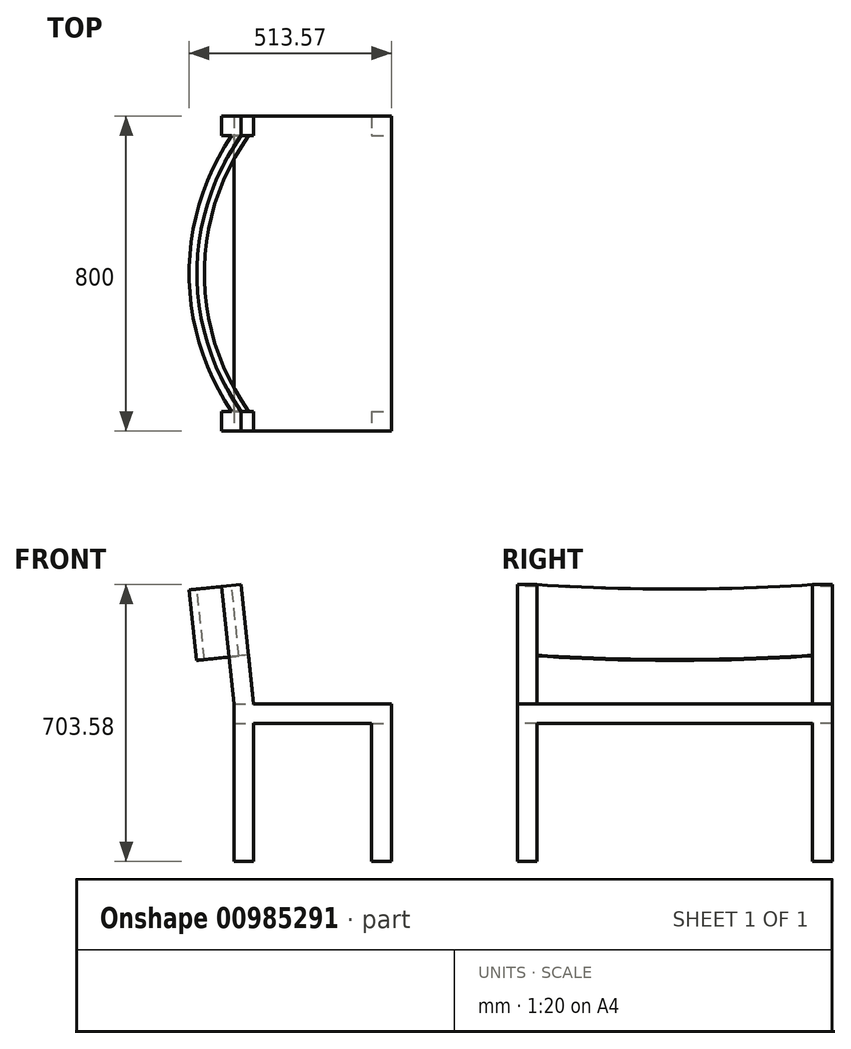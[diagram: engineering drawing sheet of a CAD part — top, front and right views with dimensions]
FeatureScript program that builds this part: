
annotation { "Feature Type Name" : "Feature", "Feature Type Description" : "" }
export const myFeature = defineFeature(function(context is Context, id is Id, definition is map)
    precondition{}
    {
        {
            var Q0;
            Q0=qCreatedBy(makeId("Top.planeOp"),FACE);
            var sketch = newSketch(context, id + "F0", { "sketchPlane" : qUnion([Q0])});
            skLineSegment(sketch, "E0.bottom", {"start": v(200, 400) * mm, "end": v(-200, 400) * mm});
            skLineSegment(sketch, "E0.top", {"start": v(200, -400) * mm, "end": v(-200, -400) * mm});
            skLineSegment(sketch, "E0.left", {"start": v(200, 400) * mm, "end": v(200, -400) * mm});
            skLineSegment(sketch, "E0.right", {"start": v(-200, 400) * mm, "end": v(-200, -400) * mm});
            skPoint(sketch, "E0.middle", {"position": v(0, 0) * mm});
            skSolve(sketch);
        }
        {
            var Q0;
            Q0=makeQuery(id+"F0.imprint","IMPRINT",FACE,{"disambiguationData":[TD([[makeQuery(id+"F0.imprint","IMPRINT",EDGE,{"derivedFrom":sQuery(id+"F0.wireOp",EDGE,"E0.bottom")}),1.0]])]});
            extrude(context, id + "F1", {"entities" : qUnion([Q0]), "depth" : 400 * mm, "offsetDistance" : 25 * mm});
        }
        {
            var Q0;
            Q0=makeQuery(id+"F1.opExtrude","SWEPT_FACE",FACE,{"disambiguationData":[OSD([sQuery(id+"F0.wireOp",EDGE,"E0.top")])]});
            var sketch = newSketch(context, id + "F2", { "sketchPlane" : qUnion([Q0])});
            skLineSegment(sketch, "E1.bottom", {"start": v(-150, 0) * mm, "end": v(150, 0) * mm});
            skLineSegment(sketch, "E1.top", {"start": v(-150, 350) * mm, "end": v(150, 350) * mm});
            skLineSegment(sketch, "E1.left", {"start": v(-150, 0) * mm, "end": v(-150, 350) * mm});
            skLineSegment(sketch, "E1.right", {"start": v(150, 0) * mm, "end": v(150, 350) * mm});
            skSolve(sketch);
        }
        {
            var Q0;
            Q0=makeQuery(id+"F2.imprint","IMPRINT",FACE,{"disambiguationData":[TD([[makeQuery(id+"F2.imprint","IMPRINT",EDGE,{"derivedFrom":sQuery(id+"F2.wireOp",EDGE,"E1.bottom")}),-1.0]])]});
            extrude(context, id + "F3", {"entities" : qUnion([Q0]), "operationType" : NewBodyOperationType.REMOVE, "endBound" : BoundingType.THROUGH_ALL, "oppositeDirection" : true, "depth" : 25 * mm, "offsetDistance" : 25 * mm});
        }
        {
            var Q0;
            Q0=makeQuery(id+"F1.opExtrude","SWEPT_FACE",FACE,{"disambiguationData":[OSD([sQuery(id+"F0.wireOp",EDGE,"E0.left")])]});
            var sketch = newSketch(context, id + "F4", { "sketchPlane" : qUnion([Q0])});
            skLineSegment(sketch, "E2.bottom", {"start": v(-350, 0) * mm, "end": v(350, 0) * mm});
            skLineSegment(sketch, "E2.top", {"start": v(-350, 350) * mm, "end": v(350, 350) * mm});
            skLineSegment(sketch, "E2.left", {"start": v(-350, 0) * mm, "end": v(-350, 350) * mm});
            skLineSegment(sketch, "E2.right", {"start": v(350, 0) * mm, "end": v(350, 350) * mm});
            skSolve(sketch);
        }
        {
            var Q0;
            Q0=makeQuery(id+"F4.imprint","IMPRINT",FACE,{"disambiguationData":[TD([[makeQuery(id+"F4.imprint","IMPRINT",EDGE,{"derivedFrom":sQuery(id+"F4.wireOp",EDGE,"E2.bottom")}),-1.0]])]});
            extrude(context, id + "F5", {"entities" : qUnion([Q0]), "operationType" : NewBodyOperationType.REMOVE, "endBound" : BoundingType.THROUGH_ALL, "oppositeDirection" : true, "depth" : 25 * mm, "offsetDistance" : 25 * mm});
        }
        {
            var Q0;
            Q0=makeQuery(id+"F1.opExtrude","CAP_FACE",FACE,{"disambiguationData":[OSD([sQuery(id+"F0.wireOp",EDGE,"E0.bottom"),sQuery(id+"F0.wireOp",EDGE,"E0.top"),sQuery(id+"F0.wireOp",EDGE,"E0.left"),sQuery(id+"F0.wireOp",EDGE,"E0.right")])],"isStart":false});
            var Q1;
            Q1=makeQuery(id+"F1.opExtrude","CAP_VERTEX",VERTEX,{"disambiguationData":[OSD([sQuery(id+"F0.wireOp",EDGE,"E0.top"),sQuery(id+"F0.wireOp",EDGE,"E0.left")])],"isStart":false});
            cPlane(context, id + "F6", {"entities" : qUnion([Q0, Q1]), "cplaneType" : CPlaneType.PLANE_POINT, "offset" : 25 * mm, "width" : 150 * mm, "height" : 150 * mm});
        }
        {
            var Q0;
            Q0=qCreatedBy(id+"F6.planeOp",FACE);
            var sketch = newSketch(context, id + "F7", { "sketchPlane" : qUnion([Q0])});
            skLineSegment(sketch, "E3", {"start": v(-200, -527.76) * mm, "end": v(-200, 626.76) * mm, "construction": true});
            skSolve(sketch);
        }
        {
            var Q0;
            Q0=makeQuery(id+"F1.opExtrude","SWEPT_FACE",FACE,{"disambiguationData":[OSD([sQuery(id+"F0.wireOp",EDGE,"E0.right")])]});
            var Q1;
            Q1=makeQuery(id+"F5.boolean.opBoolean","INTERSECT",VERTEX,{"derivedFrom":[makeQuery(id+"F1.opExtrude","SWEPT_FACE",FACE,{"disambiguationData":[OSD([sQuery(id+"F0.wireOp",EDGE,"E0.right")])]}),makeQuery(id+"F5.opExtrude","SWEPT_FACE",FACE,{"disambiguationData":[OSD([sQuery(id+"F4.wireOp",EDGE,"E2.top")])]}),makeQuery(id+"F5.opExtrude","SWEPT_FACE",FACE,{"disambiguationData":[OSD([sQuery(id+"F4.wireOp",EDGE,"E2.left")])]})]});
            cPlane(context, id + "F8", {"entities" : qUnion([Q0, Q1]), "cplaneType" : CPlaneType.PLANE_POINT, "offset" : 25 * mm, "width" : 150 * mm, "height" : 150 * mm});
        }
        {
            var Q0;
            Q0=sQuery(id+"F7.wireOp",EDGE,"E3");
            var Q1;
            Q1=qCreatedBy(id+"F8.planeOp",FACE);
            cPlane(context, id + "F9", {"entities" : qUnion([Q0, Q1]), "cplaneType" : CPlaneType.LINE_ANGLE, "offset" : 25 * mm, "angle" : 6 * degree, "oppositeDirection" : true, "width" : 150 * mm, "height" : 150 * mm});
        }
        {
            var Q0;
            Q0=qCreatedBy(id+"F9.planeOp",FACE);
            var sketch = newSketch(context, id + "F10", { "sketchPlane" : qUnion([Q0])});
            skLineSegment(sketch, "E4.bottom", {"start": v(400, 418.71) * mm, "end": v(-400, 418.71) * mm});
            skLineSegment(sketch, "E4.top", {"start": v(400, 718.71) * mm, "end": v(-400, 718.71) * mm});
            skLineSegment(sketch, "E4.left", {"start": v(400, 418.71) * mm, "end": v(400, 718.71) * mm});
            skLineSegment(sketch, "E4.right", {"start": v(-400, 418.71) * mm, "end": v(-400, 718.71) * mm});
            skSolve(sketch);
        }
        {
            var Q0;
            Q0=makeQuery(id+"F10.imprint","IMPRINT",FACE,{"disambiguationData":[TD([[makeQuery(id+"F10.imprint","IMPRINT",EDGE,{"derivedFrom":sQuery(id+"F10.wireOp",EDGE,"E4.bottom")}),-1.0]])]});
            extrude(context, id + "F11", {"entities" : qUnion([Q0]), "depth" : 50 * mm, "offsetDistance" : 25 * mm});
        }
        {
            var Q0;
            Q0=makeQuery(id+"F11.opExtrude","CAP_FACE",FACE,{"disambiguationData":[OSD([sQuery(id+"F10.wireOp",EDGE,"E4.bottom"),sQuery(id+"F10.wireOp",EDGE,"E4.top"),sQuery(id+"F10.wireOp",EDGE,"E4.left"),sQuery(id+"F10.wireOp",EDGE,"E4.right")])],"isStart":true});
            var sketch = newSketch(context, id + "F12", { "sketchPlane" : qUnion([Q0])});
            skLineSegment(sketch, "E5.bottom", {"start": v(-350, 418.71) * mm, "end": v(350, 418.71) * mm});
            skLineSegment(sketch, "E5.top", {"start": v(-350, 718.71) * mm, "end": v(350, 718.71) * mm});
            skLineSegment(sketch, "E5.left", {"start": v(-350, 418.71) * mm, "end": v(-350, 718.71) * mm});
            skLineSegment(sketch, "E5.right", {"start": v(350, 418.71) * mm, "end": v(350, 718.71) * mm});
            skSolve(sketch);
        }
        {
            var Q0;
            Q0=makeQuery(id+"F12.imprint","IMPRINT",FACE,{"disambiguationData":[TD([[makeQuery(id+"F12.imprint","IMPRINT",EDGE,{"derivedFrom":sQuery(id+"F12.wireOp",EDGE,"E5.bottom")}),1.0]])]});
            extrude(context, id + "F13", {"entities" : qUnion([Q0]), "operationType" : NewBodyOperationType.REMOVE, "endBound" : BoundingType.THROUGH_ALL, "oppositeDirection" : true, "depth" : 25 * mm, "offsetDistance" : 25 * mm});
        }
        {
            var Q0;
            {var subQ0=sQuery(id+"F10.wireOp",EDGE,"E4.right");var subQ3=sQuery(id+"F10.wireOp",EDGE,"E4.bottom");Q0=makeQuery(id+"F13.boolean.opBoolean","SPLIT",FACE,{"disambiguationData":[TD([makeQuery(id+"F11.opExtrude","SWEPT_FACE",FACE,{"disambiguationData":[OSD([subQ0])]})])],"derivedFrom":makeQuery(id+"F11.opExtrude","SWEPT_FACE",FACE,{"disambiguationData":[OSD([subQ3])]})});}
            var Q1;
            Q1=makeQuery(id+"F1.opExtrude","SWEPT_BODY",BODY,{"disambiguationData":[OSD([sQuery(id+"F0.wireOp",EDGE,"E0.bottom"),sQuery(id+"F0.wireOp",EDGE,"E0.top"),sQuery(id+"F0.wireOp",EDGE,"E0.left"),sQuery(id+"F0.wireOp",EDGE,"E0.right")])]});
            extrude(context, id + "F14", {"entities" : qUnion([Q0]), "operationType" : NewBodyOperationType.ADD, "endBound" : BoundingType.UP_TO_BODY, "depth" : 25 * mm, "endBoundEntityBody" : qUnion([Q1]), "offsetDistance" : 25 * mm});
        }
        {
            var Q0;
            {var subQ1=sQuery(id+"F10.wireOp",EDGE,"E4.left");var subQ3=sQuery(id+"F10.wireOp",EDGE,"E4.bottom");Q0=makeQuery(id+"F13.boolean.opBoolean","SPLIT",FACE,{"disambiguationData":[TD([makeQuery(id+"F11.opExtrude","SWEPT_FACE",FACE,{"disambiguationData":[OSD([subQ1])]})])],"derivedFrom":makeQuery(id+"F11.opExtrude","SWEPT_FACE",FACE,{"disambiguationData":[OSD([subQ3])]})});}
            var Q1;
            Q1=makeQuery(id+"F1.opExtrude","SWEPT_BODY",BODY,{"disambiguationData":[OSD([sQuery(id+"F0.wireOp",EDGE,"E0.bottom"),sQuery(id+"F0.wireOp",EDGE,"E0.top"),sQuery(id+"F0.wireOp",EDGE,"E0.left"),sQuery(id+"F0.wireOp",EDGE,"E0.right")])]});
            extrude(context, id + "F15", {"entities" : qUnion([Q0]), "operationType" : NewBodyOperationType.ADD, "endBound" : BoundingType.UP_TO_BODY, "depth" : 25 * mm, "endBoundEntityBody" : qUnion([Q1]), "offsetDistance" : 25 * mm});
        }
        {
            var Q0;
            {var subQ1=sQuery(id+"F10.wireOp",EDGE,"E4.left");var subQ2=sQuery(id+"F10.wireOp",EDGE,"E4.top");Q0=makeQuery(id+"F13.boolean.opBoolean","SPLIT",FACE,{"disambiguationData":[TD([makeQuery(id+"F11.opExtrude","SWEPT_FACE",FACE,{"disambiguationData":[OSD([subQ1])]})])],"derivedFrom":makeQuery(id+"F11.opExtrude","SWEPT_FACE",FACE,{"disambiguationData":[OSD([subQ2])]})});}
            var Q1;
            Q1=makeQuery(id+"F13.boolean.opBoolean","COPY",VERTEX,{"derivedFrom":makeQuery(id+"F13.opExtrude","CAP_VERTEX",VERTEX,{"disambiguationData":[OSD([sQuery(id+"F10.wireOp",EDGE,"E4.top"),sQuery(id+"F12.wireOp",EDGE,"E5.top"),sQuery(id+"F12.wireOp",EDGE,"E5.left")])],"isStart":true})});
            cPlane(context, id + "F16", {"entities" : qUnion([Q0, Q1]), "cplaneType" : CPlaneType.PLANE_POINT, "offset" : 25 * mm, "width" : 150 * mm, "height" : 150 * mm});
        }
        {
            var Q0;
            Q0=qCreatedBy(id+"F16.planeOp",FACE);
            var sketch = newSketch(context, id + "F17", { "sketchPlane" : qUnion([Q0])});
            skArc(sketch, "E6", {"start": v(-107.1, 350) * mm, "mid": v(-219.75, 0) * mm, "end": v(-107.1, -350) * mm});
            skArc(sketch, "E7.0", {"start": v(-123.34, 361.67) * mm, "mid": v(-239.75, 0) * mm, "end": v(-123.34, -361.67) * mm});
            skLineSegment(sketch, "E8", {"start": v(-107.1, 350) * mm, "end": v(-123.34, 361.67) * mm});
            skLineSegment(sketch, "E9", {"start": v(-123.34, -361.67) * mm, "end": v(-107.1, -350) * mm});
            skSolve(sketch);
        }
        {
            var Q0;
            Q0=makeQuery(id+"F17.imprint","IMPRINT",FACE,{"disambiguationData":[TD([[makeQuery(id+"F17.imprint","IMPRINT",EDGE,{"derivedFrom":sQuery(id+"F17.wireOp",EDGE,"E6")}),-1.0]])]});
            extrude(context, id + "F18", {"entities" : qUnion([Q0]), "operationType" : NewBodyOperationType.ADD, "oppositeDirection" : true, "depth" : 180 * mm, "offsetDistance" : 25 * mm});
        }
    });
